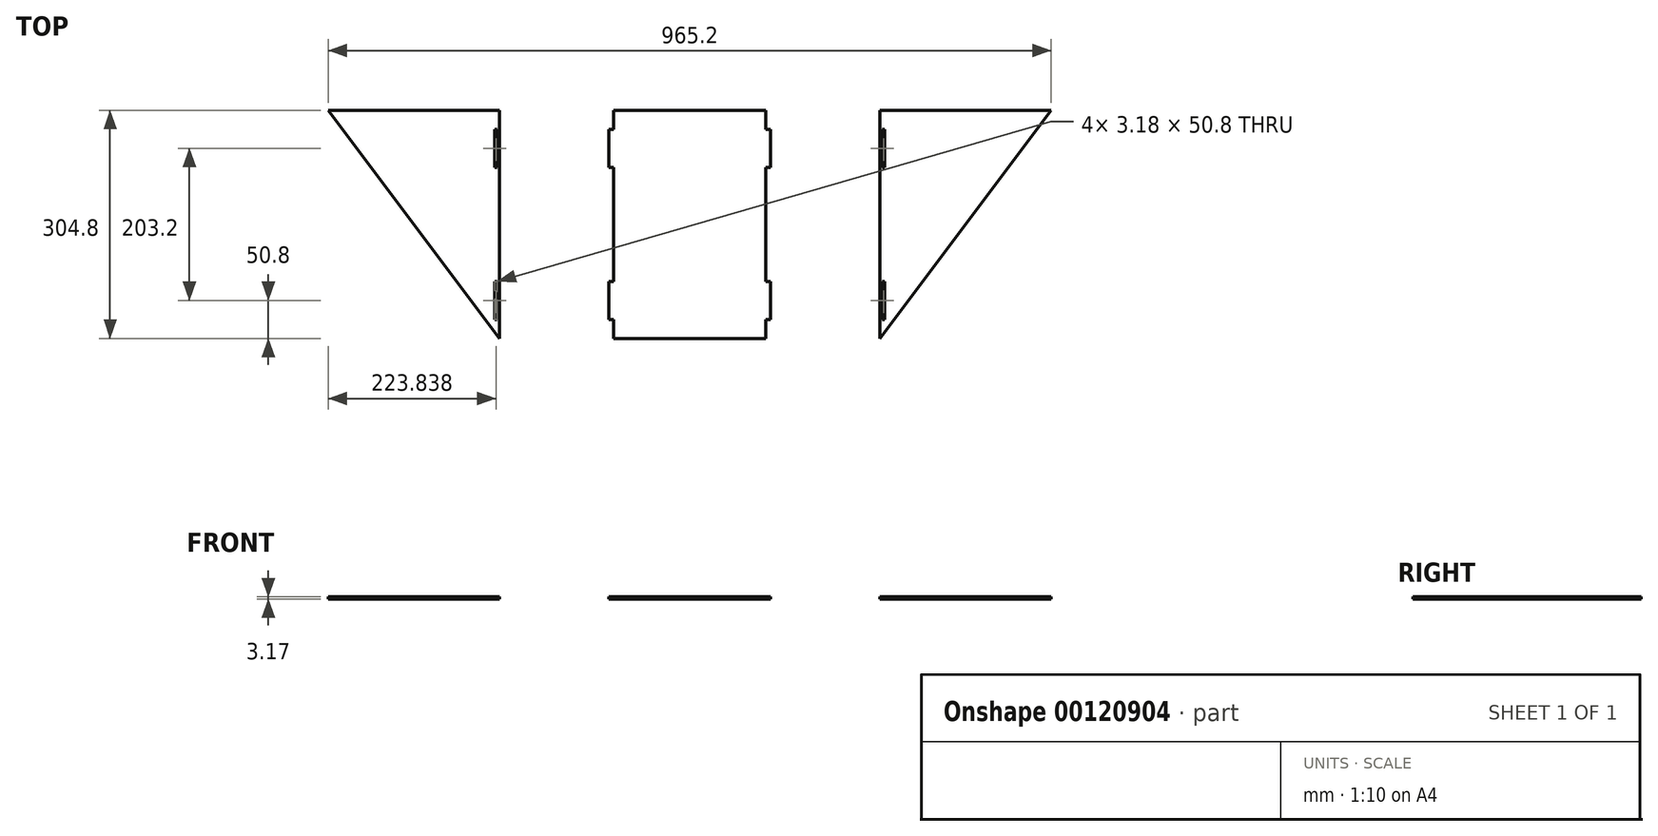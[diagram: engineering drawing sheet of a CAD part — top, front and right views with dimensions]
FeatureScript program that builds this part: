
annotation { "Feature Type Name" : "Feature", "Feature Type Description" : "" }
export const myFeature = defineFeature(function(context is Context, id is Id, definition is map)
    precondition{}
    {
        {
            var Q0;
            Q0=qCreatedBy(makeId("Top.planeOp"),FACE);
            var sketch = newSketch(context, id + "F0", { "sketchPlane" : qUnion([Q0])});
            skLineSegment(sketch, "E0", {"start": v(0, 152.4) * mm, "end": v(101.6, 152.4) * mm});
            skLineSegment(sketch, "E1", {"start": v(101.6, 152.4) * mm, "end": v(101.6, 127) * mm});
            skLineSegment(sketch, "E2", {"start": v(101.6, 127) * mm, "end": v(107.95, 127) * mm});
            skLineSegment(sketch, "E3", {"start": v(107.95, 127) * mm, "end": v(107.95, 76.2) * mm});
            skLineSegment(sketch, "E4", {"start": v(107.95, 76.2) * mm, "end": v(101.6, 76.2) * mm});
            skLineSegment(sketch, "E5", {"start": v(101.6, 76.2) * mm, "end": v(101.6, 0) * mm});
            skLineSegment(sketch, "E6.MirrorCS", {"start": v(0, -152.4) * mm, "end": v(101.6, -152.4) * mm});
            skLineSegment(sketch, "E7.MirrorCS", {"start": v(101.6, -152.4) * mm, "end": v(101.6, -127) * mm});
            skLineSegment(sketch, "E8.MirrorCS", {"start": v(107.95, -127) * mm, "end": v(107.95, -76.2) * mm});
            skLineSegment(sketch, "E9.MirrorCS", {"start": v(101.6, -127) * mm, "end": v(107.95, -127) * mm});
            skLineSegment(sketch, "E10.MirrorCS", {"start": v(107.95, -76.2) * mm, "end": v(101.6, -76.2) * mm});
            skLineSegment(sketch, "E11.MirrorCS", {"start": v(101.6, -76.2) * mm, "end": v(101.6, 0) * mm});
            skLineSegment(sketch, "E12.MirrorCS", {"start": v(-101.6, 152.4) * mm, "end": v(-101.6, 127) * mm});
            skLineSegment(sketch, "E13.MirrorCS", {"start": v(-107.95, -76.2) * mm, "end": v(-101.6, -76.2) * mm});
            skLineSegment(sketch, "E14.MirrorCS", {"start": v(-101.6, -127) * mm, "end": v(-107.95, -127) * mm});
            skLineSegment(sketch, "E15.MirrorCS", {"start": v(-101.6, 127) * mm, "end": v(-107.95, 127) * mm});
            skLineSegment(sketch, "E16.MirrorCS", {"start": v(-107.95, 76.2) * mm, "end": v(-101.6, 76.2) * mm});
            skLineSegment(sketch, "E17.MirrorCS", {"start": v(-101.6, -152.4) * mm, "end": v(-101.6, -127) * mm});
            skLineSegment(sketch, "E18.MirrorCS", {"start": v(0, 152.4) * mm, "end": v(-101.6, 152.4) * mm});
            skLineSegment(sketch, "E19.MirrorCS", {"start": v(-101.6, -76.2) * mm, "end": v(-101.6, 0) * mm});
            skLineSegment(sketch, "E20.MirrorCS", {"start": v(0, -152.4) * mm, "end": v(-101.6, -152.4) * mm});
            skLineSegment(sketch, "E21.MirrorCS", {"start": v(-101.6, 76.2) * mm, "end": v(-101.6, 0) * mm});
            skLineSegment(sketch, "E22.MirrorCS", {"start": v(-107.95, -127) * mm, "end": v(-107.95, -76.2) * mm});
            skLineSegment(sketch, "E23.MirrorCS", {"start": v(-107.95, 127) * mm, "end": v(-107.95, 76.2) * mm});
            skLineSegment(sketch, "E24", {"start": v(254, -152.4) * mm, "end": v(254, 152.4) * mm});
            skLineSegment(sketch, "E25", {"start": v(254, -152.4) * mm, "end": v(482.6, 152.4) * mm});
            skLineSegment(sketch, "E26", {"start": v(254, 152.4) * mm, "end": v(482.6, 152.4) * mm});
            skLineSegment(sketch, "E27.bottom", {"start": v(257.17, 76.2) * mm, "end": v(260.35, 76.2) * mm});
            skLineSegment(sketch, "E27.top", {"start": v(257.17, 127) * mm, "end": v(260.35, 127) * mm});
            skLineSegment(sketch, "E27.left", {"start": v(257.17, 76.2) * mm, "end": v(257.17, 127) * mm});
            skLineSegment(sketch, "E27.right", {"start": v(260.35, 76.2) * mm, "end": v(260.35, 127) * mm});
            skLineSegment(sketch, "E28.bottom", {"start": v(257.18, -127) * mm, "end": v(260.35, -127) * mm});
            skLineSegment(sketch, "E28.top", {"start": v(257.18, -76.2) * mm, "end": v(260.35, -76.2) * mm});
            skLineSegment(sketch, "E28.left", {"start": v(257.18, -127) * mm, "end": v(257.18, -76.2) * mm});
            skLineSegment(sketch, "E28.right", {"start": v(260.35, -127) * mm, "end": v(260.35, -76.2) * mm});
            skLineSegment(sketch, "E29.MirrorCS", {"start": v(-257.17, 127) * mm, "end": v(-260.35, 127) * mm});
            skLineSegment(sketch, "E30.MirrorCS", {"start": v(-257.17, 76.2) * mm, "end": v(-260.35, 76.2) * mm});
            skLineSegment(sketch, "E31.MirrorCS", {"start": v(-257.18, -76.2) * mm, "end": v(-260.35, -76.2) * mm});
            skLineSegment(sketch, "E32.MirrorCS", {"start": v(-257.18, -127) * mm, "end": v(-260.35, -127) * mm});
            skLineSegment(sketch, "E33.MirrorCS", {"start": v(-257.17, 76.2) * mm, "end": v(-257.17, 127) * mm});
            skLineSegment(sketch, "E34.MirrorCS", {"start": v(-254, -152.4) * mm, "end": v(-482.6, 152.4) * mm});
            skLineSegment(sketch, "E35.MirrorCS", {"start": v(-257.18, -127) * mm, "end": v(-257.18, -76.2) * mm});
            skLineSegment(sketch, "E36.MirrorCS", {"start": v(-260.35, 76.2) * mm, "end": v(-260.35, 127) * mm});
            skLineSegment(sketch, "E37.MirrorCS", {"start": v(-254, -152.4) * mm, "end": v(-254, 152.4) * mm});
            skLineSegment(sketch, "E38.MirrorCS", {"start": v(-260.35, -127) * mm, "end": v(-260.35, -76.2) * mm});
            skLineSegment(sketch, "E39.MirrorCS", {"start": v(-254, 152.4) * mm, "end": v(-482.6, 152.4) * mm});
            skSolve(sketch);
        }
        {
            var Q0;
            Q0=makeQuery(id+"F0.imprint","IMPRINT",FACE,{"disambiguationData":[TD([[makeQuery(id+"F0.imprint","IMPRINT",EDGE,{"derivedFrom":sQuery(id+"F0.wireOp",EDGE,"E0")}),-1.0]])]});
            var Q1;
            Q1=makeQuery(id+"F0.imprint","IMPRINT",FACE,{"disambiguationData":[TD([[makeQuery(id+"F0.imprint","IMPRINT",EDGE,{"derivedFrom":sQuery(id+"F0.wireOp",EDGE,"E29.MirrorCS")}),-1.0]])]});
            var Q2;
            Q2=makeQuery(id+"F0.imprint","IMPRINT",FACE,{"disambiguationData":[TD([[makeQuery(id+"F0.imprint","IMPRINT",EDGE,{"derivedFrom":sQuery(id+"F0.wireOp",EDGE,"E24")}),-1.0]])]});
            extrude(context, id + "F1", {"entities" : qUnion([Q0, Q1, Q2]), "depth" : 3.17 * mm});
        }
    });
